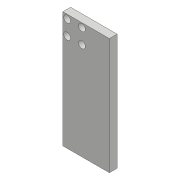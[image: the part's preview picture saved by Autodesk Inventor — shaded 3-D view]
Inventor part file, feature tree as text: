
AUTODESK INVENTOR PART (.ipt)
format: ipt  version: 2018 (Build 220112000, 112)  size: 109,568 bytes
history: native  units: mm
features: projected_geometry x5, extrude x3, sketch x3
ambient origin geometry x8: Origin, YZ Plane, XZ Plane, XY Plane, X Axis, Y Axis, Z Axis, Center Point
bodies: Solid1 (feature_tree)
feature tree (11):
  extrude  "Extrusion1"  Depth=44.0mm
  extrude  "Extrusion2"  Depth=7.3mm
  extrude  "Extrusion3"  Depth=6.7mm
  sketch  "Sketch1"  dims[d0=110.0mm d1=44.0mm]
  sketch  "Sketch2"  dims[d2=7.3mm d3=0.0mm d4=22.0mm]
  projected_geometry  "Projected Loop1"
  sketch  "Sketch3"  dims[d5=22.0mm d6=14.0mm d7=7.5mm d8=6.7mm d9=0.0mm d10=6.7mm d11=0.0mm d12=6.5mm d13=6.5mm d14=6.5mm d15=6.5mm]
  projected_geometry  "Projected Loop2"
  projected_geometry  "Projected Loop3"
  projected_geometry  "Projected Loop4"
  projected_geometry  "Projected Loop5"
